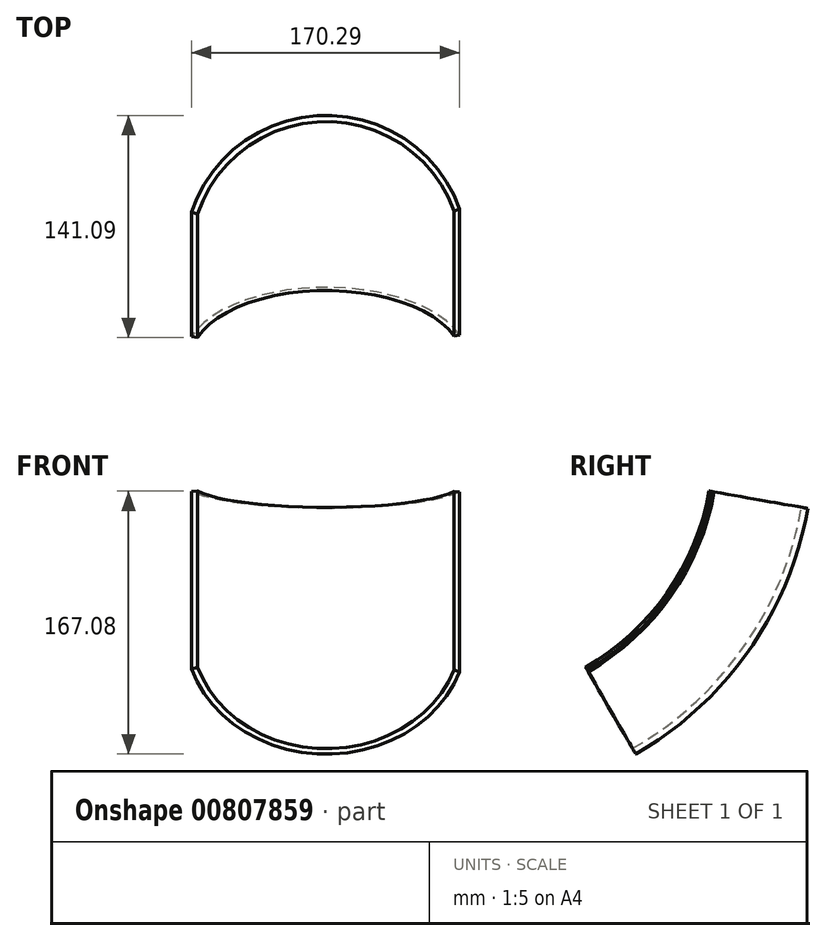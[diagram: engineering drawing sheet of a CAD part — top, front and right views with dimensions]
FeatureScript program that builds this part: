
annotation { "Feature Type Name" : "Feature", "Feature Type Description" : "" }
export const myFeature = defineFeature(function(context is Context, id is Id, definition is map)
    precondition{}
    {
        {
            var Q0;
            Q0=qCreatedBy(makeId("Front.planeOp"),FACE);
            var sketch = newSketch(context, id + "F0", { "sketchPlane" : qUnion([Q0])});
            skLineSegment(sketch, "E0", {"start": v(-109.57, 0) * mm, "end": v(134.88, 0) * mm});
            skPoint(sketch, "E1.middle", {"position": v(0, 0) * mm});
            skArc(sketch, "E2", {"start": v(75, 162.53) * mm, "mid": v(-0.66, 215) * mm, "end": v(-75, 160.68) * mm});
            skLineSegment(sketch, "E3", {"start": v(-75, 160.68) * mm, "end": v(-75, 0) * mm});
            skLineSegment(sketch, "E4", {"start": v(75, 162.53) * mm, "end": v(75, 0) * mm});
            skSolve(sketch);
        }
        {
            var Q0;
            Q0=qCreatedBy(makeId("Front.planeOp"),FACE);
            var sketch = newSketch(context, id + "F1", { "sketchPlane" : qUnion([Q0])});
            skArc(sketch, "E5.3", {"start": v(81.35, 163.62) * mm, "mid": v(-0.7, 221.34) * mm, "end": v(-81.35, 161.68) * mm});
            skArc(sketch, "E6.0", {"start": v(85.13, 164.92) * mm, "mid": v(-0.74, 225.34) * mm, "end": v(-85.16, 162.9) * mm});
            skLineSegment(sketch, "E7", {"start": v(-85.16, 162.9) * mm, "end": v(-81.35, 161.68) * mm});
            skLineSegment(sketch, "E8", {"start": v(81.35, 163.62) * mm, "end": v(85.13, 164.92) * mm});
            skSolve(sketch);
        }
        {
            var Q0;
            Q0=qSketchRegion(id+"F1",true);
            var Q1;
            Q1=sQuery(id+"F0.wireOp",EDGE,"E0");
            revolve(context, id + "F2", {"surfaceOperationType" : NewSurfaceOperationType.NEW, "entities" : qUnion([Q0]), "axis" : qUnion([Q1]), "revolveType" : RevolveType.TWO_DIRECTIONS, "angle" : 260 * degree, "angleBack" : 210 * degree});
        }
    });
